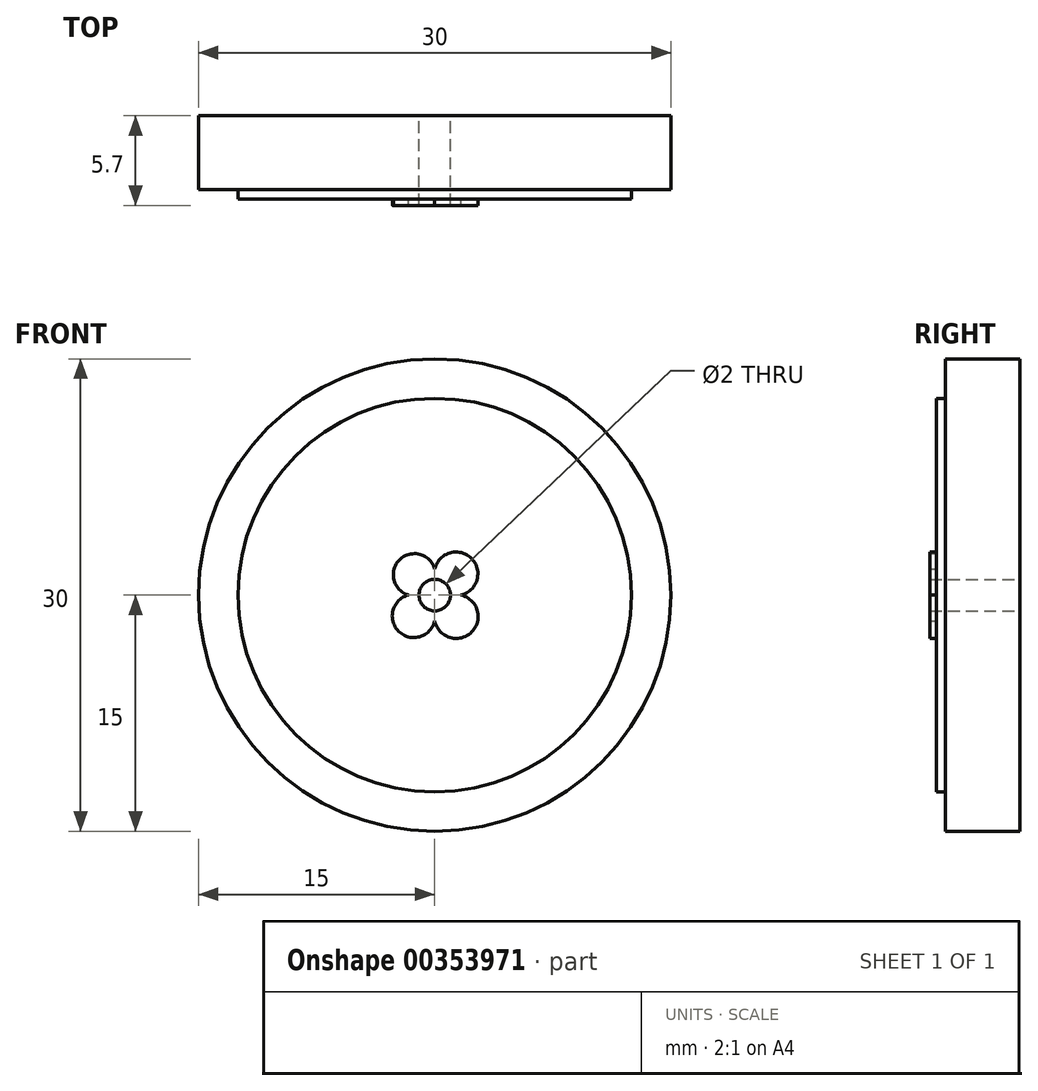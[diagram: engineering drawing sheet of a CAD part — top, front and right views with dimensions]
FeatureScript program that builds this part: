
annotation { "Feature Type Name" : "Feature", "Feature Type Description" : "" }
export const myFeature = defineFeature(function(context is Context, id is Id, definition is map)
    precondition{}
    {
        {
            var Q0;
            Q0=qCreatedBy(makeId("Front.planeOp"),FACE);
            var sketch = newSketch(context, id + "F0", { "sketchPlane" : qUnion([Q0])});
            skCircle(sketch, "E0", {"center": v(0, 0) * mm, "radius": 15 * mm});
            skCircle(sketch, "E1", {"center": v(0, 0) * mm, "radius": 1 * mm});
            skCircle(sketch, "E2", {"center": v(0, 0) * mm, "radius": 12.5 * mm});
            skSolve(sketch);
        }
        {
            var Q0;
            Q0=makeQuery(id+"F0.imprint","IMPRINT",FACE,{"disambiguationData":[TD([[makeQuery(id+"F0.imprint","IMPRINT",EDGE,{"derivedFrom":sQuery(id+"F0.wireOp",EDGE,"E0")}),1.0]])]});
            extrude(context, id + "F1", {"entities" : qUnion([Q0]), "depth" : 4.7 * mm});
        }
        {
            var Q0;
            Q0=makeQuery(id+"F0.imprint","IMPRINT",FACE,{"disambiguationData":[TD([[makeQuery(id+"F0.imprint","IMPRINT",EDGE,{"derivedFrom":sQuery(id+"F0.wireOp",EDGE,"E1")}),-1.0]])]});
            extrude(context, id + "F2", {"entities" : qUnion([Q0]), "operationType" : NewBodyOperationType.ADD, "depth" : 5.3 * mm});
        }
        {
            var Q0;
            Q0=makeQuery(id+"F2.opExtrude","CAP_FACE",FACE,{"disambiguationData":[OSD([sQuery(id+"F0.wireOp",EDGE,"E1"),sQuery(id+"F0.wireOp",EDGE,"E2")])],"isStart":false});
            var sketch = newSketch(context, id + "F3", { "sketchPlane" : qUnion([Q0])});
            skArc(sketch, "E3", {"start": v(-1.66, 0) * mm, "mid": v(-2.3, -2.3) * mm, "end": v(0, -1.66) * mm});
            skArc(sketch, "E4", {"start": v(0, 1.66) * mm, "mid": v(-2.24, 2.24) * mm, "end": v(-1.66, 0) * mm});
            skArc(sketch, "E5", {"start": v(0, -1.66) * mm, "mid": v(2.35, -2.35) * mm, "end": v(1.66, 0) * mm});
            skArc(sketch, "E6", {"start": v(1.66, 0) * mm, "mid": v(2.33, 2.33) * mm, "end": v(0, 1.66) * mm});
            skPoint(sketch, "E7.start.orphan", {"position": v(0, 1) * mm});
            skPoint(sketch, "E8.orphan", {"position": v(-1, 0) * mm});
            skPoint(sketch, "E9.orphan", {"position": v(0, -1) * mm});
            skSolve(sketch);
        }
        {
            var Q0;
            {var subQ0=sQuery(id+"F3.wireOp",EDGE,"E7");var subQ1=sQuery(id+"F3.wireOp",EDGE,"E3");var subQ2=makeQuery(id+"F3.imprint","INTERSECT",VERTEX,{"derivedFrom":[subQ1,subQ0]});Q0=makeQuery(id+"F3.imprint","IMPRINT",FACE,{"disambiguationData":[TD([[makeQuery(id+"F3.imprint","IMPRINT",EDGE,{"disambiguationData":[TD([[subQ2,-1.0]])],"derivedFrom":subQ1}),1.0]])]});}
            var Q1;
            {var subQ0=sQuery(id+"F3.wireOp",EDGE,"5UZdQIGJ-yLW9-Mggl-2CMM-rQs0AN2eFA2S");var subQ1=sQuery(id+"F3.wireOp",EDGE,"E3");var subQ4=makeQuery(id+"F3.imprint","INTERSECT",VERTEX,{"derivedFrom":[subQ1,subQ0]});Q1=makeQuery(id+"F3.imprint","IMPRINT",FACE,{"disambiguationData":[TD([[makeQuery(id+"F3.imprint","IMPRINT",EDGE,{"disambiguationData":[TD([[subQ4,-1.0]])],"derivedFrom":subQ0}),1.0]])]});}
            var Q2;
            {var subQ0=sQuery(id+"F3.wireOp",EDGE,"n87LNbUK-0wL7-6WXv-wtKE-NlyvgdZ460SN");var subQ1=sQuery(id+"F3.wireOp",EDGE,"5UZdQIGJ-yLW9-Mggl-2CMM-rQs0AN2eFA2S");var subQ4=makeQuery(id+"F3.imprint","INTERSECT",VERTEX,{"derivedFrom":[subQ1,subQ0]});Q2=makeQuery(id+"F3.imprint","IMPRINT",FACE,{"disambiguationData":[TD([[makeQuery(id+"F3.imprint","IMPRINT",EDGE,{"disambiguationData":[TD([[subQ4,-1.0]])],"derivedFrom":subQ0}),1.0]])]});}
            var Q3;
            {var subQ0=sQuery(id+"F3.wireOp",EDGE,"E7");var subQ1=sQuery(id+"F3.wireOp",EDGE,"E3");var subQ4=makeQuery(id+"F3.imprint","INTERSECT",VERTEX,{"derivedFrom":[subQ1,subQ0]});Q3=makeQuery(id+"F3.imprint","IMPRINT",FACE,{"disambiguationData":[TD([[makeQuery(id+"F3.imprint","IMPRINT",EDGE,{"disambiguationData":[TD([[subQ4,1.0]])],"derivedFrom":subQ0}),1.0]])]});}
            extrude(context, id + "F4", {"entities" : qUnion([Q0, Q1, Q2, Q3]), "operationType" : NewBodyOperationType.ADD, "depth" : 0.4 * mm});
        }
    });
